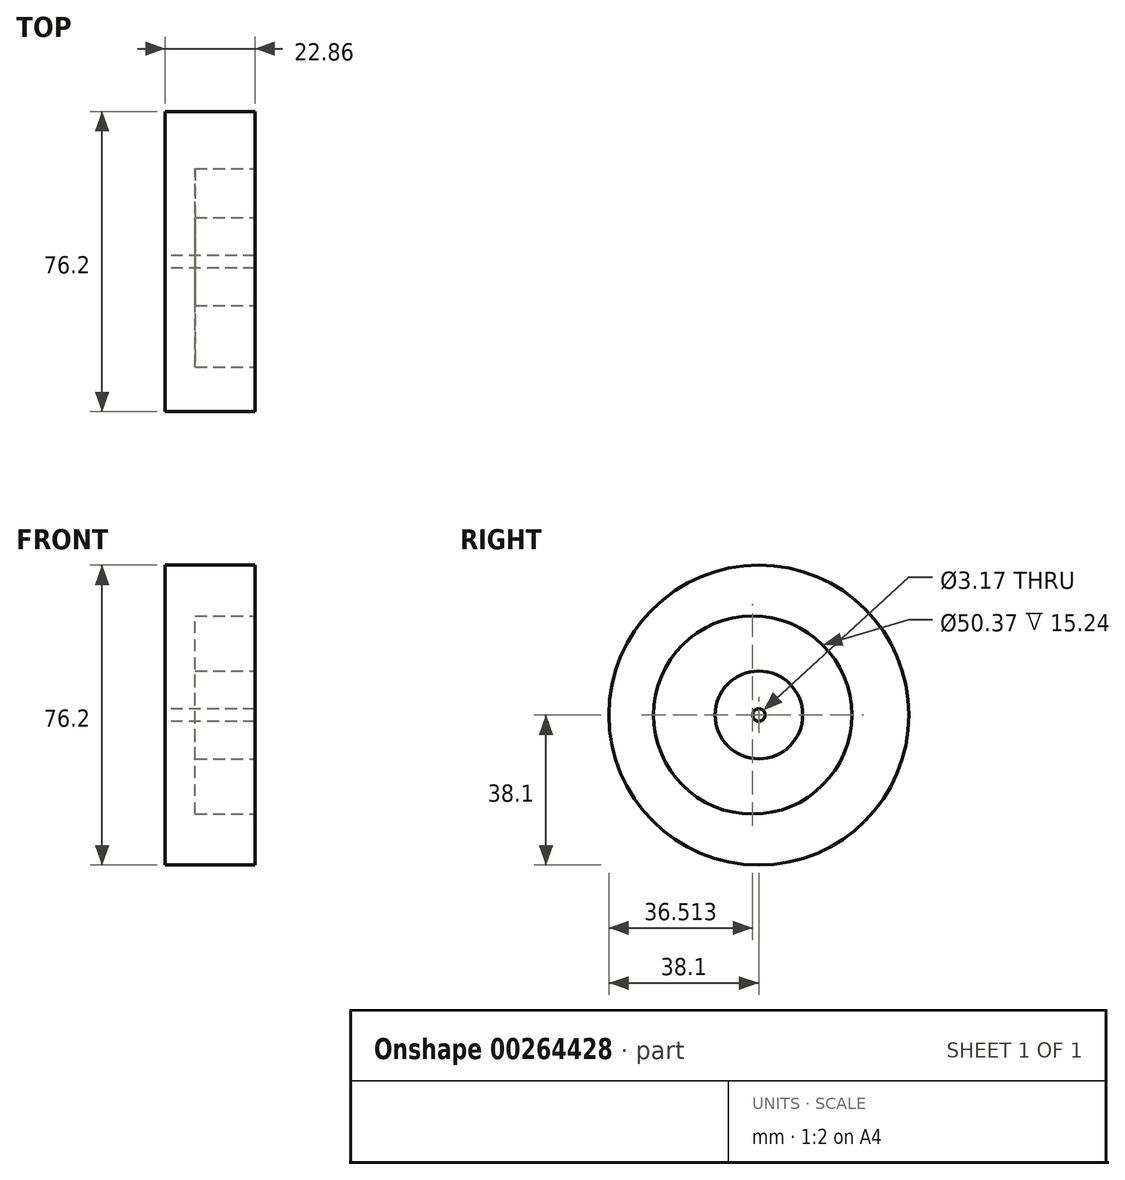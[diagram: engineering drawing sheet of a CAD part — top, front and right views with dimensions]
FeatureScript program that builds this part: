
annotation { "Feature Type Name" : "Feature", "Feature Type Description" : "" }
export const myFeature = defineFeature(function(context is Context, id is Id, definition is map)
    precondition{}
    {
        {
            var Q0;
            Q0=qCreatedBy(makeId("Right.planeOp"),FACE);
            var sketch = newSketch(context, id + "F0", { "sketchPlane" : qUnion([Q0])});
            skCircle(sketch, "E0", {"center": v(0, 0) * mm, "radius": 38.1 * mm});
            skCircle(sketch, "E1", {"center": v(0, 0) * mm, "radius": 1.59 * mm});
            skSolve(sketch);
        }
        {
            var Q0;
            Q0=makeQuery(id+"F0.imprint","IMPRINT",FACE,{"disambiguationData":[TD([[makeQuery(id+"F0.imprint","IMPRINT",EDGE,{"derivedFrom":sQuery(id+"F0.wireOp",EDGE,"E0")}),1.0]])]});
            extrude(context, id + "F1", {"entities" : qUnion([Q0]), "depth" : 22.86 * mm});
        }
        {
            var Q0;
            Q0=makeQuery(id+"F1.opExtrude","CAP_FACE",FACE,{"disambiguationData":[OSD([sQuery(id+"F0.wireOp",EDGE,"E0"),sQuery(id+"F0.wireOp",EDGE,"E1")])],"isStart":false});
            var sketch = newSketch(context, id + "F2", { "sketchPlane" : qUnion([Q0])});
            skCircle(sketch, "E2", {"center": v(-1.59, 0) * mm, "radius": 25.18 * mm});
            skCircle(sketch, "E3", {"center": v(0, 0) * mm, "radius": 11.14 * mm});
            skSolve(sketch);
        }
        {
            var Q0;
            Q0 = qSketchRegion(id + "F2", true);
            extrude(context, id + "F3", {"entities" : qUnion([Q0]), "operationType" : NewBodyOperationType.REMOVE, "oppositeDirection" : true, "depth" : 15.24 * mm});
        }
    });
